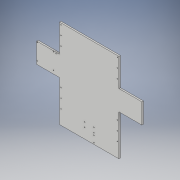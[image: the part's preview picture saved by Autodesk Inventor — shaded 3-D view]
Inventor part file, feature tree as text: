
AUTODESK INVENTOR PART (.ipt)
format: ipt  version: 2019 (Build 230136000, 136)  size: 225,792 bytes
history: native  units: in
note: dims shown in document units (in); Inventor stores cm internally (conversion verified against a paired STEP export)
features: extrude x5, sketch x5, plane x2
ambient origin geometry x8: Origin, YZ Plane, XZ Plane, XY Plane, X Axis, Y Axis, Z Axis, Center Point
bodies: Solid1 (feature_tree)
feature tree (12):
  plane  "Work Plane32"
  extrude  "Extrusion20"  Depth=0.25in TaperAngle=0.0deg
  plane  "Work Plane28"
  extrude  "Extrusion21"  Depth=3.25in
  extrude  "Extrusion22"  Depth=0.2in
  extrude  "Extrusion23"  Depth=0.2in
  extrude  "Extrusion24"  Depth=0.25in
  sketch  "Sketch36"  dims[d408=0.25in d409=0.0in d410=0.25in d411=0.0in]
  sketch  "Sketch38"  dims[d412=3.25in d413=10.0in]
  sketch  "Sketch39"  dims[d414=1.25in d415=0.2in]
  sketch  "Sketch40"  dims[d416=0.2in d417=0.2in]
  sketch  "Sketch41"  dims[d418=0.25in d419=0.0in d420=0.25in d421=0.25in d422=1.5in d423=1.5in d424=0.25in d425=0.25in d426=1.5in d427=1.5in d428=2.3in d429=1.5in d430=1.5in d431=0.25in d432=0.25in d433=0.25in d434=0.14in d435=0.14in d436=0.14in d437=0.14in d438=0.14in d439=0.14in d440=0.14in d441=0.14in d442=0.14in d443=0.14in d444=0.14in d445=0.14in d446=0.25in d447=0.0in d448=1.45in d449=0.25in d450=0.0in d284=1.0in d285=1.0in]
